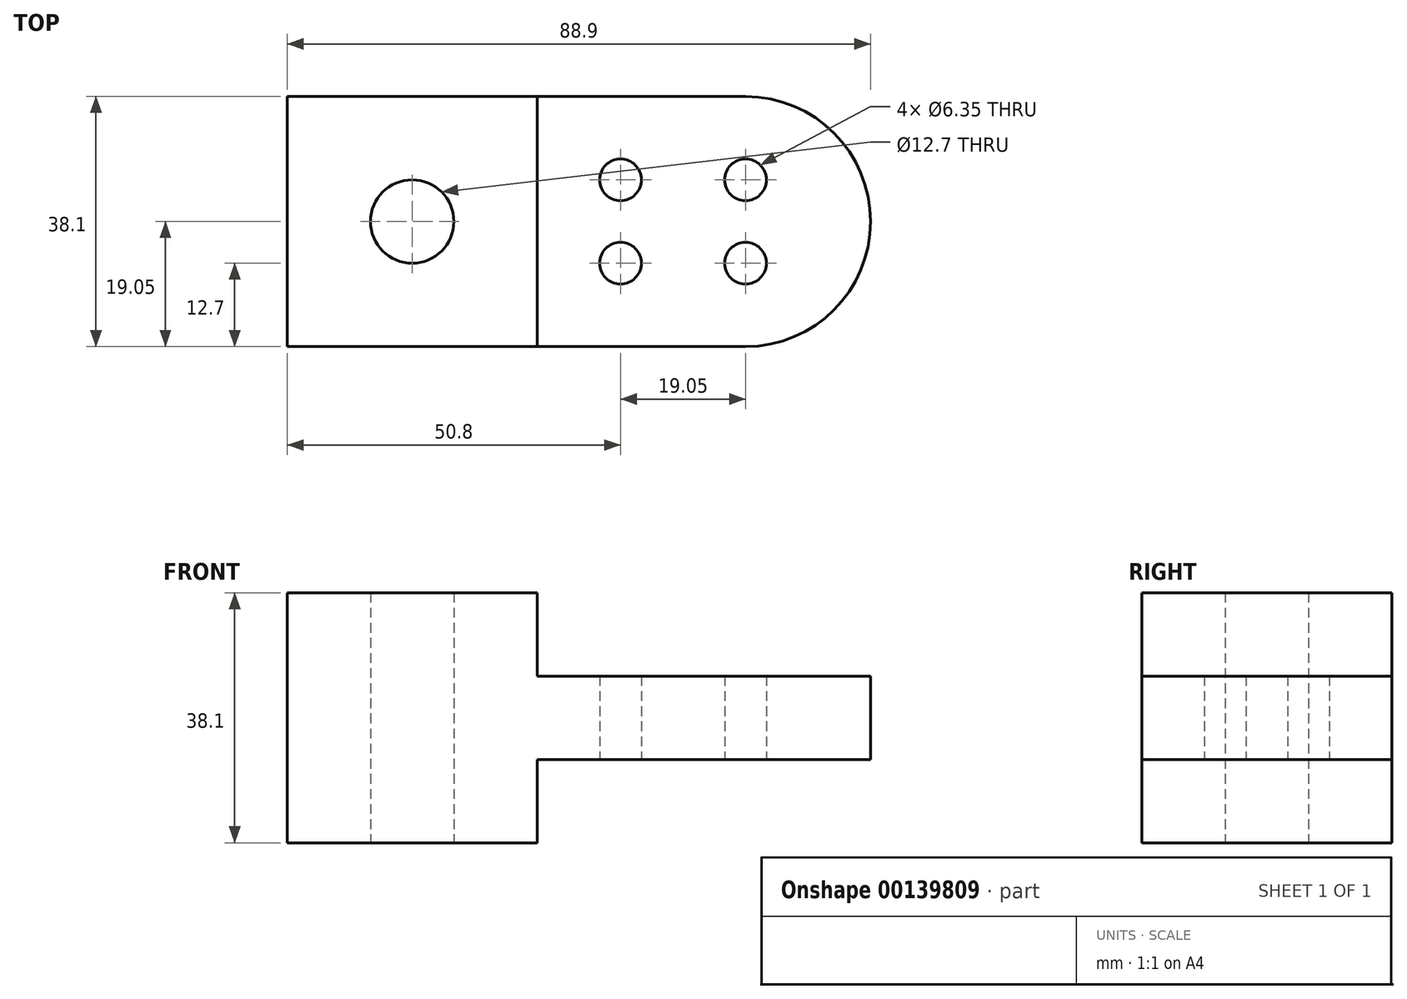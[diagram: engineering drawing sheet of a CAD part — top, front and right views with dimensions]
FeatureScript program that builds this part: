
annotation { "Feature Type Name" : "Feature", "Feature Type Description" : "" }
export const myFeature = defineFeature(function(context is Context, id is Id, definition is map)
    precondition{}
    {
        {
            var Q0;
            Q0=qCreatedBy(makeId("Top.planeOp"),FACE);
            var sketch = newSketch(context, id + "F0", { "sketchPlane" : qUnion([Q0])});
            skLineSegment(sketch, "E0.bottom", {"start": v(19.05, -19.05) * mm, "end": v(-19.05, -19.05) * mm});
            skLineSegment(sketch, "E0.top", {"start": v(19.05, 19.05) * mm, "end": v(-19.05, 19.05) * mm});
            skLineSegment(sketch, "E0.left", {"start": v(19.05, -19.05) * mm, "end": v(19.05, 19.05) * mm});
            skLineSegment(sketch, "E0.right", {"start": v(-19.05, -19.05) * mm, "end": v(-19.05, 19.05) * mm});
            skPoint(sketch, "E0.middle", {"position": v(0, 0) * mm});
            skSolve(sketch);
        }
        {
            var Q0;
            Q0 = qSketchRegion(id + "F0", true);
            extrude(context, id + "F1", {"entities" : qUnion([Q0]), "endBound" : BoundingType.SYMMETRIC, "depth" : 38.1 * mm});
        }
        {
            var Q0;
            Q0=qCreatedBy(makeId("Top.planeOp"),FACE);
            var sketch = newSketch(context, id + "F2", { "sketchPlane" : qUnion([Q0])});
            skCircle(sketch, "E1", {"center": v(0, 0) * mm, "radius": 6.35 * mm});
            skSolve(sketch);
        }
        {
            var Q0;
            Q0 = qSketchRegion(id + "F2", true);
            extrude(context, id + "F3", {"entities" : qUnion([Q0]), "operationType" : NewBodyOperationType.REMOVE, "endBound" : BoundingType.SYMMETRIC, "depth" : 38.1 * mm});
        }
        {
            var Q0;
            Q0=qCreatedBy(makeId("Top.planeOp"),FACE);
            var sketch = newSketch(context, id + "F4", { "sketchPlane" : qUnion([Q0])});
            skLineSegment(sketch, "E2.0", {"start": v(19.05, -19.05) * mm, "end": v(19.05, 19.05) * mm});
            skLineSegment(sketch, "E3.bottom", {"start": v(19.05, 19.05) * mm, "end": v(50.8, 19.05) * mm});
            skLineSegment(sketch, "E3.top", {"start": v(19.05, -19.05) * mm, "end": v(50.8, -19.05) * mm});
            skLineSegment(sketch, "E3.left", {"start": v(19.05, 19.05) * mm, "end": v(19.05, -19.05) * mm});
            skArc(sketch, "E4", {"start": v(50.8, -19.05) * mm, "mid": v(69.85, 0) * mm, "end": v(50.8, 19.05) * mm});
            skLineSegment(sketch, "E5", {"start": v(50.8, 0) * mm, "end": v(50.8, 6.35) * mm, "construction": true});
            skLineSegment(sketch, "E6", {"start": v(50.8, 6.35) * mm, "end": v(31.75, 6.35) * mm, "construction": true});
            skLineSegment(sketch, "E7", {"start": v(31.75, 6.35) * mm, "end": v(31.75, -6.35) * mm, "construction": true});
            skLineSegment(sketch, "E8", {"start": v(31.75, -6.35) * mm, "end": v(50.8, -6.35) * mm, "construction": true});
            skCircle(sketch, "E9", {"center": v(50.8, -6.35) * mm, "radius": 3.18 * mm});
            skCircle(sketch, "E10", {"center": v(50.8, 6.35) * mm, "radius": 3.18 * mm});
            skCircle(sketch, "E11", {"center": v(31.75, 6.35) * mm, "radius": 3.18 * mm});
            skCircle(sketch, "E12", {"center": v(31.75, -6.35) * mm, "radius": 3.18 * mm});
            skSolve(sketch);
        }
        {
            var Q0;
            Q0 = qSketchRegion(id + "F4", true);
            extrude(context, id + "F5", {"entities" : qUnion([Q0]), "operationType" : NewBodyOperationType.ADD, "endBound" : BoundingType.SYMMETRIC, "depth" : 12.7 * mm});
        }
    });
